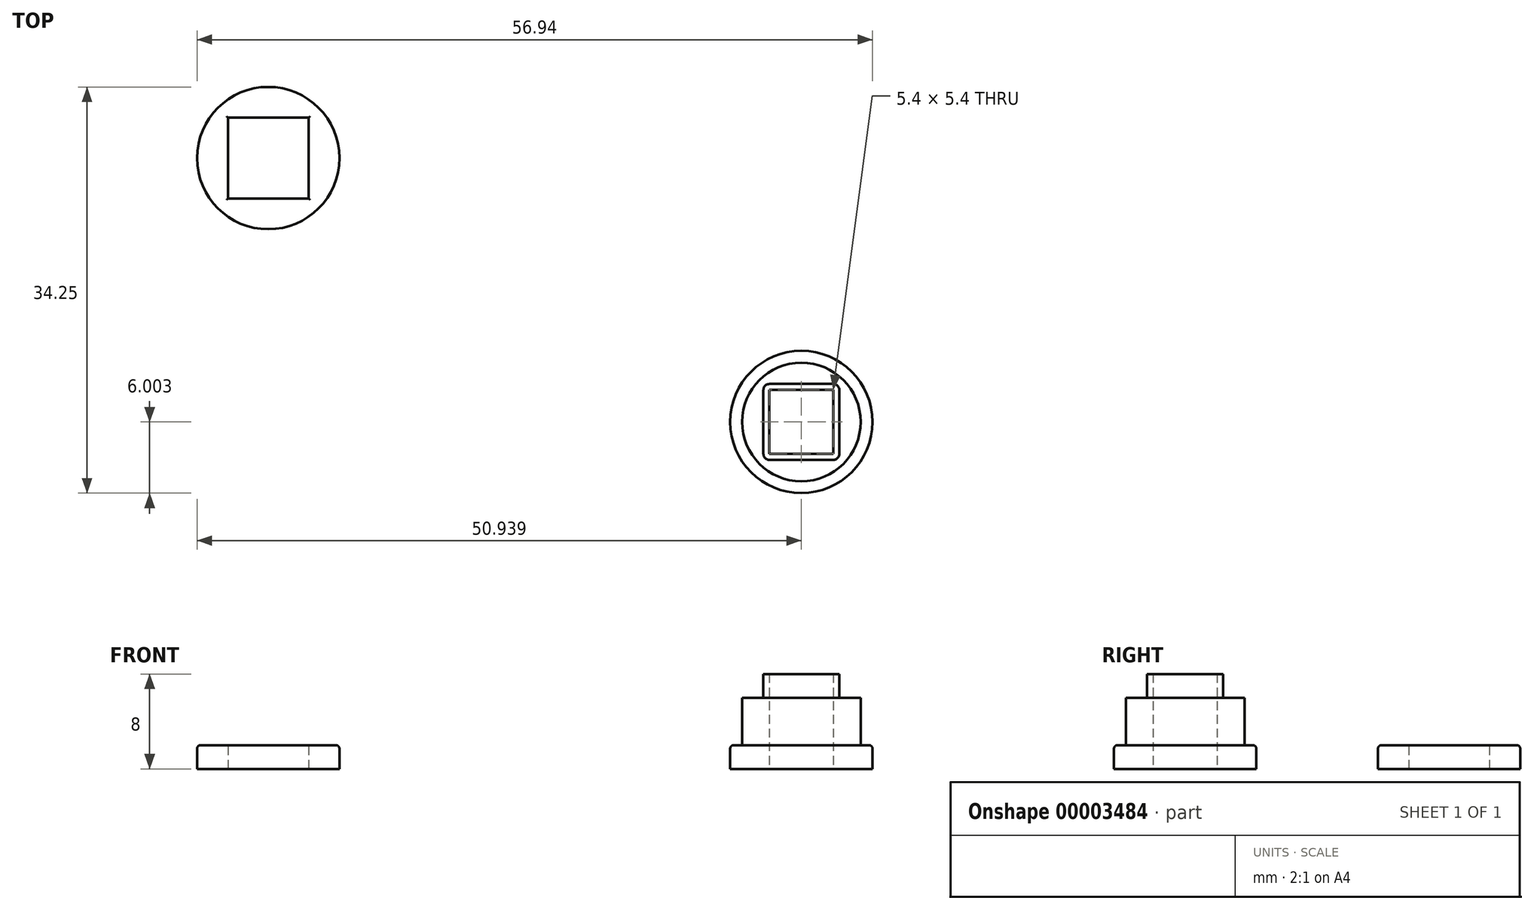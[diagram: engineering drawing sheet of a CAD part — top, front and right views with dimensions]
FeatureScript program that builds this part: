
annotation { "Feature Type Name" : "Feature", "Feature Type Description" : "" }
export const myFeature = defineFeature(function(context is Context, id is Id, definition is map)
    precondition{}
    {
        {
            var Q0;
            Q0=qCreatedBy(makeId("Top.planeOp"),FACE);
            var sketch = newSketch(context, id + "F0", { "sketchPlane" : qUnion([Q0])});
            skCircle(sketch, "E0", {"center": v(-45, 27.18) * mm, "radius": 5 * mm});
            skCircle(sketch, "E1", {"center": v(-45, 27.18) * mm, "radius": 6 * mm});
            skLineSegment(sketch, "E2.rect.bottom", {"start": v(-42.3, 29.88) * mm, "end": v(-47.7, 29.88) * mm});
            skLineSegment(sketch, "E2.rect.top", {"start": v(-42.3, 24.48) * mm, "end": v(-47.7, 24.48) * mm});
            skLineSegment(sketch, "E2.rect.left", {"start": v(-42.3, 29.88) * mm, "end": v(-42.3, 24.48) * mm});
            skLineSegment(sketch, "E2.rect.right", {"start": v(-47.7, 29.88) * mm, "end": v(-47.7, 24.48) * mm});
            skLineSegment(sketch, "E3.0", {"start": v(-41.8, 30.38) * mm, "end": v(-48.2, 30.38) * mm});
            skLineSegment(sketch, "E3.1", {"start": v(-41.8, 30.38) * mm, "end": v(-41.8, 23.98) * mm});
            skLineSegment(sketch, "E3.2", {"start": v(-41.8, 23.98) * mm, "end": v(-48.2, 23.98) * mm});
            skLineSegment(sketch, "E3.3", {"start": v(-48.2, 30.38) * mm, "end": v(-48.2, 23.98) * mm});
            skSolve(sketch);
        }
        {
            var Q0;
            Q0=makeQuery(id+"F0.imprint","IMPRINT",FACE,{"disambiguationData":[TD([[makeQuery(id+"F0.imprint","IMPRINT",EDGE,{"derivedFrom":sQuery(id+"F0.wireOp",EDGE,"E0")}),1.0]])]});
            var Q1;
            Q1=makeQuery(id+"F0.imprint","IMPRINT",FACE,{"disambiguationData":[TD([[makeQuery(id+"F0.imprint","IMPRINT",EDGE,{"derivedFrom":sQuery(id+"F0.wireOp",EDGE,"E0")}),-1.0]])]});
            var Q2;
            Q2=makeQuery(id+"F0.imprint","IMPRINT",FACE,{"disambiguationData":[TD([[makeQuery(id+"F0.imprint","IMPRINT",EDGE,{"derivedFrom":sQuery(id+"F0.wireOp",EDGE,"E2.rect.bottom")}),-1.0]])]});
            extrude(context, id + "F1", {"entities" : qUnion([Q0, Q1, Q2]), "depth" : 2 * mm});
        }
        {
            var Q0;
            Q0=makeQuery(id+"F0.imprint","IMPRINT",FACE,{"disambiguationData":[TD([[makeQuery(id+"F0.imprint","IMPRINT",EDGE,{"derivedFrom":sQuery(id+"F0.wireOp",EDGE,"E0")}),1.0]])]});
            var Q1;
            Q1=makeQuery(id+"F0.imprint","IMPRINT",FACE,{"disambiguationData":[TD([[makeQuery(id+"F0.imprint","IMPRINT",EDGE,{"derivedFrom":sQuery(id+"F0.wireOp",EDGE,"E2.rect.bottom")}),-1.0]])]});
            extrude(context, id + "F2", {"entities" : qUnion([Q0, Q1]), "operationType" : NewBodyOperationType.ADD, "depth" : 6 * mm});
        }
        {
            var Q0;
            Q0=makeQuery(id+"F0.imprint","IMPRINT",FACE,{"disambiguationData":[TD([[makeQuery(id+"F0.imprint","IMPRINT",EDGE,{"derivedFrom":sQuery(id+"F0.wireOp",EDGE,"E2.rect.bottom")}),-1.0]])]});
            extrude(context, id + "F3", {"entities" : qUnion([Q0]), "operationType" : NewBodyOperationType.ADD, "depth" : 8 * mm});
        }
        {
            var Q0;
            Q0=makeQuery(id+"F1.opExtrude","SWEPT_BODY",BODY,{"disambiguationData":[OSD([sQuery(id+"F0.wireOp",EDGE,"E1"),sQuery(id+"F0.wireOp",EDGE,"E2.rect.bottom"),sQuery(id+"F0.wireOp",EDGE,"E2.rect.top"),sQuery(id+"F0.wireOp",EDGE,"E2.rect.left"),sQuery(id+"F0.wireOp",EDGE,"E2.rect.right")])]});
            transform(context, id + "F4", {"entities" : qUnion([Q0]), "transformType" : TransformType.TRANSLATION_3D, "dx" : 27.23 * mm, "dy" : -5.5 * mm, "dz" : 0 * mm, "makeCopy" : false});
        }
        {
            var Q0;
            Q0=makeQuery(id+"F3.opExtrude","SWEPT_EDGE",EDGE,{"disambiguationData":[OSD([sQuery(id+"F0.wireOp",EDGE,"E3.2"),sQuery(id+"F0.wireOp",EDGE,"E3.3")])]});
            var Q1;
            Q1=makeQuery(id+"F3.opExtrude","SWEPT_EDGE",EDGE,{"disambiguationData":[OSD([sQuery(id+"F0.wireOp",EDGE,"E3.1"),sQuery(id+"F0.wireOp",EDGE,"E3.2")])]});
            var Q2;
            Q2=makeQuery(id+"F3.opExtrude","SWEPT_EDGE",EDGE,{"disambiguationData":[OSD([sQuery(id+"F0.wireOp",EDGE,"E3.0"),sQuery(id+"F0.wireOp",EDGE,"E3.3")])]});
            var Q3;
            Q3=makeQuery(id+"F3.opExtrude","SWEPT_EDGE",EDGE,{"disambiguationData":[OSD([sQuery(id+"F0.wireOp",EDGE,"E3.0"),sQuery(id+"F0.wireOp",EDGE,"E3.1")])]});
            fillet(context, id + "F5", {"entities" : qUnion([Q0, Q1, Q2, Q3]), "radius" : 0.5 * mm, "tangentPropagation" : true, "allowEdgeOverflow" : false});
        }
        {
            var Q0;
            Q0=qCreatedBy(makeId("Top.planeOp"),FACE);
            var sketch = newSketch(context, id + "F6", { "sketchPlane" : qUnion([Q0])});
            skCircle(sketch, "E4", {"center": v(-62.7, 43.92) * mm, "radius": 6 * mm});
            skLineSegment(sketch, "E5.rect.bottom", {"start": v(-59.3, 40.52) * mm, "end": v(-66.1, 40.52) * mm});
            skLineSegment(sketch, "E5.rect.top", {"start": v(-59.3, 47.32) * mm, "end": v(-66.1, 47.32) * mm});
            skLineSegment(sketch, "E5.rect.left", {"start": v(-59.3, 40.52) * mm, "end": v(-59.3, 47.32) * mm});
            skLineSegment(sketch, "E5.rect.right", {"start": v(-66.1, 40.52) * mm, "end": v(-66.1, 47.32) * mm});
            skSolve(sketch);
        }
        {
            var Q0;
            Q0=makeQuery(id+"F6.imprint","IMPRINT",FACE,{"disambiguationData":[TD([[makeQuery(id+"F6.imprint","IMPRINT",EDGE,{"derivedFrom":sQuery(id+"F6.wireOp",EDGE,"E4")}),1.0]])]});
            extrude(context, id + "F7", {"entities" : qUnion([Q0]), "depth" : 2 * mm});
        }
        {
            var Q0;
            Q0=makeQuery(id+"F7.opExtrude","CAP_EDGE",EDGE,{"disambiguationData":[OSD([sQuery(id+"F6.wireOp",EDGE,"E5.rect.top")])],"isStart":false});
            var Q1;
            Q1=makeQuery(id+"F7.opExtrude","CAP_EDGE",EDGE,{"disambiguationData":[OSD([sQuery(id+"F6.wireOp",EDGE,"E5.rect.right")])],"isStart":false});
            var Q2;
            Q2=makeQuery(id+"F7.opExtrude","CAP_EDGE",EDGE,{"disambiguationData":[OSD([sQuery(id+"F6.wireOp",EDGE,"E5.rect.bottom")])],"isStart":false});
            var Q3;
            Q3=makeQuery(id+"F7.opExtrude","CAP_EDGE",EDGE,{"disambiguationData":[OSD([sQuery(id+"F6.wireOp",EDGE,"E5.rect.left")])],"isStart":false});
            fillet(context, id + "F8", {"entities" : qUnion([Q0, Q1, Q2, Q3]), "radius" : 0.1 * mm, "tangentPropagation" : true, "allowEdgeOverflow" : false});
        }
        {
            var Q0;
            Q0=makeQuery(id+"F7.opExtrude","CAP_EDGE",EDGE,{"disambiguationData":[OSD([sQuery(id+"F6.wireOp",EDGE,"E4")])],"isStart":false});
            fillet(context, id + "F9", {"entities" : qUnion([Q0]), "radius" : 0.3 * mm, "tangentPropagation" : true, "allowEdgeOverflow" : false});
        }
        {
            var Q0;
            Q0=makeQuery(id+"F1.opExtrude","CAP_EDGE",EDGE,{"disambiguationData":[OSD([sQuery(id+"F0.wireOp",EDGE,"E1")])],"isStart":false});
            fillet(context, id + "F10", {"entities" : qUnion([Q0]), "radius" : 0.3 * mm, "tangentPropagation" : true, "allowEdgeOverflow" : false});
        }
    });
